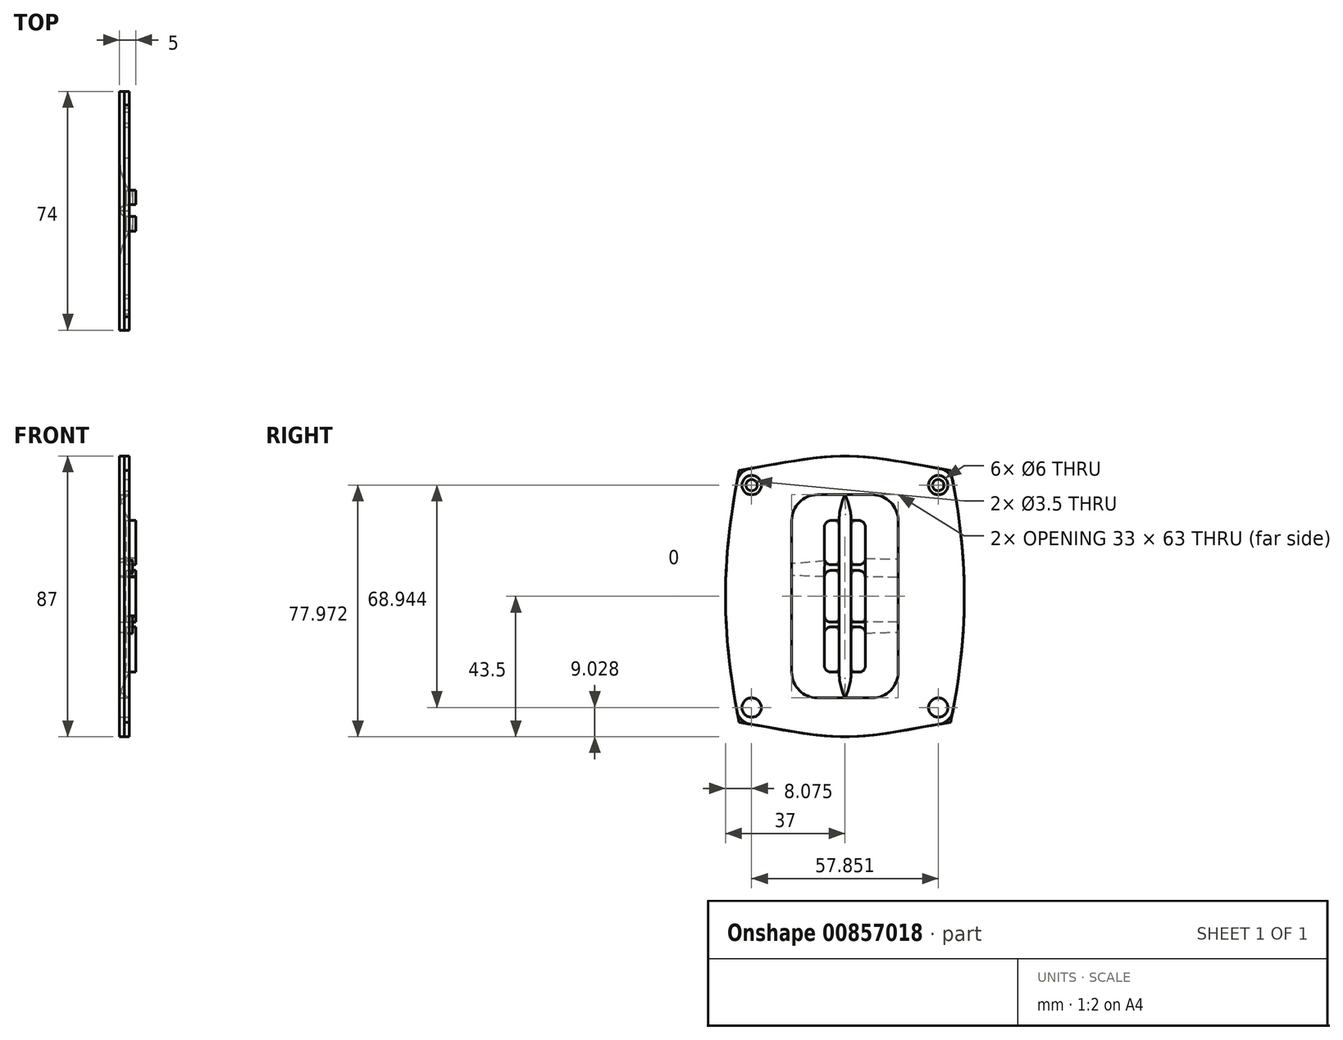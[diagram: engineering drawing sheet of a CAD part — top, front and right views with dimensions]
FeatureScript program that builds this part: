
annotation { "Feature Type Name" : "Feature", "Feature Type Description" : "" }
export const myFeature = defineFeature(function(context is Context, id is Id, definition is map)
    precondition{}
    {
        {
            var Q0;
            Q0=qCreatedBy(makeId("Right.planeOp"),FACE);
            var sketch = newSketch(context, id + "F0", { "sketchPlane" : qUnion([Q0])});
            skLineSegment(sketch, "E0", {"start": v(0, 0) * mm, "end": v(0, 31.5) * mm});
            skPoint(sketch, "E1.center", {"position": v(0, 0) * mm});
            skLineSegment(sketch, "E2", {"start": v(0, 0) * mm, "end": v(0, -31.5) * mm});
            skLineSegment(sketch, "E3.bottom", {"start": v(8.5, 31.5) * mm, "end": v(-8.5, 31.5) * mm});
            skLineSegment(sketch, "E3.top", {"start": v(8.5, -31.5) * mm, "end": v(-8.5, -31.5) * mm});
            skLineSegment(sketch, "E3.left", {"start": v(16.5, 23.5) * mm, "end": v(16.5, -23.5) * mm});
            skLineSegment(sketch, "E3.right", {"start": v(-16.5, 23.5) * mm, "end": v(-16.5, -23.5) * mm});
            skLineSegment(sketch, "E4.bottom", {"start": v(4.28, 8) * mm, "end": v(2.98, 8) * mm});
            skLineSegment(sketch, "E4.top", {"start": v(6.28, -8) * mm, "end": v(2.98, -8) * mm});
            skLineSegment(sketch, "E4.left", {"start": v(6.28, 6) * mm, "end": v(6.28, -8) * mm});
            skPoint(sketch, "E5.orphan", {"position": v(2.98, -17) * mm});
            skPoint(sketch, "E6.visualSharp", {"position": v(16.5, 31.5) * mm});
            skArc(sketch, "E6.filletArc", {"start": v(16.5, 23.5) * mm, "mid": v(14.16, 29.16) * mm, "end": v(8.5, 31.5) * mm});
            skPoint(sketch, "E7.visualSharp", {"position": v(-16.5, -31.5) * mm});
            skArc(sketch, "E7.filletArc", {"start": v(-16.5, -23.5) * mm, "mid": v(-14.16, -29.16) * mm, "end": v(-8.5, -31.5) * mm});
            skPoint(sketch, "E8.visualSharp", {"position": v(-16.5, 31.5) * mm});
            skArc(sketch, "E8.filletArc", {"start": v(-8.5, 31.5) * mm, "mid": v(-14.16, 29.16) * mm, "end": v(-16.5, 23.5) * mm});
            skPoint(sketch, "E9.visualSharp", {"position": v(16.5, -31.5) * mm});
            skArc(sketch, "E9.filletArc", {"start": v(8.5, -31.5) * mm, "mid": v(14.16, -29.16) * mm, "end": v(16.5, -23.5) * mm});
            skLineSegment(sketch, "E10.bottom", {"start": v(4.35, 23.5) * mm, "end": v(1.93, 23.5) * mm});
            skLineSegment(sketch, "E10.top", {"start": v(4.35, -23.5) * mm, "end": v(1.93, -23.5) * mm});
            skLineSegment(sketch, "E10.left", {"start": v(6.35, 21.5) * mm, "end": v(6.35, 11.8) * mm});
            skLineSegment(sketch, "E10.right", {"start": v(-6.35, 21.5) * mm, "end": v(-6.35, 11.8) * mm});
            skLineSegment(sketch, "E11", {"start": v(1.93, 23.5) * mm, "end": v(1.93, -23.5) * mm});
            skLineSegment(sketch, "E12", {"start": v(-1.78, -23.5) * mm, "end": v(-1.78, 23.5) * mm});
            skLineSegment(sketch, "E13", {"start": v(4.35, 9.8) * mm, "end": v(1.93, 9.8) * mm});
            skLineSegment(sketch, "E14", {"start": v(2.98, 8) * mm, "end": v(1.93, 8) * mm});
            skLineSegment(sketch, "E15", {"start": v(6.28, -8) * mm, "end": v(1.93, -8) * mm});
            skLineSegment(sketch, "E16", {"start": v(4.35, -9.47) * mm, "end": v(1.93, -9.47) * mm});
            skArc(sketch, "E17", {"start": v(1.93, 23.5) * mm, "mid": v(1.44, 27.61) * mm, "end": v(0, 31.5) * mm});
            skArc(sketch, "E18", {"start": v(0, 31.5) * mm, "mid": v(-1.33, 27.6) * mm, "end": v(-1.78, 23.5) * mm});
            skArc(sketch, "E19", {"start": v(-1.78, -23.5) * mm, "mid": v(-1.33, -27.6) * mm, "end": v(0, -31.5) * mm});
            skArc(sketch, "E20", {"start": v(0, -31.5) * mm, "mid": v(1.44, -27.61) * mm, "end": v(1.93, -23.5) * mm});
            skPoint(sketch, "E21.visualSharp", {"position": v(6.35, -23.5) * mm});
            skArc(sketch, "E21.filletArc", {"start": v(4.35, -23.5) * mm, "mid": v(5.76, -22.91) * mm, "end": v(6.35, -21.5) * mm});
            skPoint(sketch, "E22.visualSharp", {"position": v(-6.35, -23.5) * mm});
            skArc(sketch, "E22.filletArc", {"start": v(-6.35, -21.5) * mm, "mid": v(-5.76, -22.91) * mm, "end": v(-4.35, -23.5) * mm});
            skPoint(sketch, "E23.visualSharp", {"position": v(-6.35, 23.5) * mm});
            skArc(sketch, "E23.filletArc", {"start": v(-4.35, 23.5) * mm, "mid": v(-5.76, 22.91) * mm, "end": v(-6.35, 21.5) * mm});
            skPoint(sketch, "E24.visualSharp", {"position": v(6.35, 23.5) * mm});
            skArc(sketch, "E24.filletArc", {"start": v(6.35, 21.5) * mm, "mid": v(5.76, 22.91) * mm, "end": v(4.35, 23.5) * mm});
            skLineSegment(sketch, "E25.trimOffspring", {"start": v(-6.35, 6) * mm, "end": v(-6.35, -6) * mm});
            skLineSegment(sketch, "E26.trimOffspring", {"start": v(-1.78, 8) * mm, "end": v(-4.35, 8) * mm});
            skLineSegment(sketch, "E27.trimOffspring", {"start": v(-1.78, 9.8) * mm, "end": v(-4.35, 9.8) * mm});
            skLineSegment(sketch, "E28.trimOffspring", {"start": v(6.35, -11.47) * mm, "end": v(6.35, -21.5) * mm});
            skLineSegment(sketch, "E29.trimOffspring", {"start": v(-1.78, 23.5) * mm, "end": v(-4.35, 23.5) * mm});
            skLineSegment(sketch, "E30.trimOffspring", {"start": v(-6.35, -11.47) * mm, "end": v(-6.35, -21.5) * mm});
            skLineSegment(sketch, "E31.trimOffspring", {"start": v(-1.78, -8) * mm, "end": v(-4.35, -8) * mm});
            skLineSegment(sketch, "E32.trimOffspring", {"start": v(-1.78, -9.47) * mm, "end": v(-4.35, -9.47) * mm});
            skLineSegment(sketch, "E33.trimOffspring", {"start": v(-1.78, -23.5) * mm, "end": v(-4.35, -23.5) * mm});
            skPoint(sketch, "E34.visualSharp", {"position": v(6.35, -9.47) * mm});
            skArc(sketch, "E34.filletArc", {"start": v(6.35, -11.47) * mm, "mid": v(5.76, -10.05) * mm, "end": v(4.35, -9.47) * mm});
            skPoint(sketch, "E35.visualSharp", {"position": v(6.28, 8) * mm});
            skArc(sketch, "E35.filletArc", {"start": v(6.28, 6) * mm, "mid": v(5.7, 7.41) * mm, "end": v(4.28, 8) * mm});
            skPoint(sketch, "E36.visualSharp", {"position": v(-6.35, 8) * mm});
            skArc(sketch, "E36.filletArc", {"start": v(-4.35, 8) * mm, "mid": v(-5.76, 7.41) * mm, "end": v(-6.35, 6) * mm});
            skPoint(sketch, "E37.visualSharp", {"position": v(6.35, 9.8) * mm});
            skArc(sketch, "E37.filletArc", {"start": v(4.35, 9.8) * mm, "mid": v(5.76, 10.39) * mm, "end": v(6.35, 11.8) * mm});
            skPoint(sketch, "E38.visualSharp", {"position": v(-6.35, 9.8) * mm});
            skArc(sketch, "E38.filletArc", {"start": v(-6.35, 11.8) * mm, "mid": v(-5.76, 10.39) * mm, "end": v(-4.35, 9.8) * mm});
            skPoint(sketch, "E39.visualSharp", {"position": v(-6.35, -9.47) * mm});
            skArc(sketch, "E39.filletArc", {"start": v(-4.35, -9.47) * mm, "mid": v(-5.76, -10.05) * mm, "end": v(-6.35, -11.47) * mm});
            skPoint(sketch, "E40.visualSharp", {"position": v(-6.35, -8) * mm});
            skArc(sketch, "E40.filletArc", {"start": v(-6.35, -6) * mm, "mid": v(-5.76, -7.41) * mm, "end": v(-4.35, -8) * mm});
            skLineSegment(sketch, "E41", {"start": v(6.35, 11.8) * mm, "end": v(6.28, 6) * mm});
            skLineSegment(sketch, "E42", {"start": v(-6.22, 11.09) * mm, "end": v(-6.35, 6) * mm});
            skLineSegment(sketch, "E43", {"start": v(6.28, -8) * mm, "end": v(6.35, -11.47) * mm});
            skLineSegment(sketch, "E44", {"start": v(-6.35, -6) * mm, "end": v(-6.35, -6.14) * mm});
            skPoint(sketch, "E45", {"position": v(0, 43.5) * mm});
            skPoint(sketch, "E46", {"position": v(0, -43.5) * mm});
            skPoint(sketch, "E47", {"position": v(-37, 0) * mm});
            skPoint(sketch, "E48", {"position": v(37, 0) * mm});
            skLineSegment(sketch, "E49", {"start": v(6.3, 7.5) * mm, "end": v(5.95, 7.1) * mm});
            skPoint(sketch, "E50", {"position": v(28.93, 34.47) * mm});
            skCircle(sketch, "E51", {"center": v(28.93, 34.47) * mm, "radius": 3 * mm});
            skCircle(sketch, "E52", {"center": v(-28.93, 34.47) * mm, "radius": 3 * mm});
            skLineSegment(sketch, "E53", {"start": v(0, 0) * mm, "end": v(-1.78, 0) * mm});
            skLineSegment(sketch, "E54", {"start": v(-1, 0) * mm, "end": v(1.93, 0) * mm});
            skPoint(sketch, "E55.MirrorP", {"position": v(28.93, -34.47) * mm});
            skCircle(sketch, "E56.MirrorC", {"center": v(-28.93, -34.47) * mm, "radius": 3 * mm});
            skCircle(sketch, "E57.MirrorC", {"center": v(28.93, -34.47) * mm, "radius": 3 * mm});
            skPoint(sketch, "E58", {"position": v(32.78, 39.07) * mm});
            skPoint(sketch, "E59.MirrorP", {"position": v(-32.78, 39.07) * mm});
            skPoint(sketch, "E60.MirrorP", {"position": v(32.78, -39.07) * mm});
            skLineSegment(sketch, "E61", {"start": v(-6, 7.14) * mm, "end": v(-6.31, 7.52) * mm});
            skPoint(sketch, "E62.MirrorP", {"position": v(-32.78, -39.07) * mm});
            skFitSpline(sketch, "E63", {"points": [v(32.78, 39.07) * mm, v(0, 43.5) * mm, v(-32.78, 39.07) * mm], "startDerivative": vector(-65.56, 9.7) * mm, "endDerivative": vector(-65.56, -9.7) * mm});
            skFitSpline(sketch, "E64", {"points": [v(-32.78, 39.07) * mm, v(-37, 0) * mm, v(-32.78, -39.07) * mm], "startDerivative": vector(-15.65, -78.14) * mm, "endDerivative": vector(15.65, -78.14) * mm});
            skFitSpline(sketch, "E65", {"points": [v(-32.78, -39.07) * mm, v(0, -43.5) * mm, v(32.78, -39.07) * mm], "startDerivative": vector(65.56, -9.7) * mm, "endDerivative": vector(65.56, 9.7) * mm});
            skFitSpline(sketch, "E66", {"points": [v(32.78, -39.07) * mm, v(37, 0) * mm, v(32.78, 39.07) * mm], "startDerivative": vector(15.65, 78.14) * mm, "endDerivative": vector(-15.65, 78.14) * mm});
            skLineSegment(sketch, "E67", {"start": v(-6.35, -6) * mm, "end": v(-6.35, -12.75) * mm});
            skCircle(sketch, "E68", {"center": v(28.93, 34.47) * mm, "radius": 1.75 * mm});
            skCircle(sketch, "E69", {"center": v(-28.93, 34.47) * mm, "radius": 1.75 * mm});
            skCircle(sketch, "E70", {"center": v(28.93, -34.47) * mm, "radius": 1.75 * mm});
            skCircle(sketch, "E71", {"center": v(-28.93, -34.47) * mm, "radius": 1.75 * mm});
            skSolve(sketch);
        }
        {
            var Q0;
            {var subQ15=sQuery(id+"F0.wireOp",EDGE,"E6.filletArc");Q0=makeQuery(id+"F0.imprint","IMPRINT",FACE,{"disambiguationData":[TD([[makeQuery(id+"F0.imprint","IMPRINT",EDGE,{"derivedFrom":subQ15}),-1.0]])]});}
            var Q1;
            {var subQ0=sQuery(id+"F0.wireOp",EDGE,"E8.filletArc");Q1=makeQuery(id+"F0.imprint","IMPRINT",FACE,{"disambiguationData":[TD([[makeQuery(id+"F0.imprint","IMPRINT",EDGE,{"derivedFrom":subQ0}),-1.0]])]});}
            var Q2;
            {var subQ1=sQuery(id+"F0.wireOp",EDGE,"0K8LcDmi-TPdW-6mqs-PaqG-IcpSsZEtbQrD");var subQ9=sQuery(id+"F0.wireOp",EDGE,"E52");var subQ10=makeQuery(id+"F0.imprint","INTERSECT",VERTEX,{"disambiguationData":[OD(1.0)],"derivedFrom":[subQ1,subQ9]});Q2=makeQuery(id+"F0.imprint","IMPRINT",FACE,{"disambiguationData":[TD([[makeQuery(id+"F0.imprint","IMPRINT",EDGE,{"disambiguationData":[TD([[subQ10,-1.0]])],"derivedFrom":subQ1}),1.0]])]});}
            var Q3;
            {var subQ5=sQuery(id+"F0.wireOp",EDGE,"0K8LcDmi-TPdW-6mqs-PaqG-IcpSsZEtbQrD");var subQ10=sQuery(id+"F0.wireOp",EDGE,"E52");var subQ11=makeQuery(id+"F0.imprint","INTERSECT",VERTEX,{"disambiguationData":[OD(1.0)],"derivedFrom":[subQ5,subQ10]});Q3=makeQuery(id+"F0.imprint","IMPRINT",FACE,{"disambiguationData":[TD([[makeQuery(id+"F0.imprint","IMPRINT",EDGE,{"disambiguationData":[TD([[subQ11,-1.0]])],"derivedFrom":subQ5}),-1.0]])]});}
            var Q4;
            {var subQ0=sQuery(id+"F0.wireOp",EDGE,"E64");var subQ1=sQuery(id+"F0.wireOp",EDGE,"3NlvXYQv-4iI8-wcnj-cC3w-IblLpaBuwml8");var subQ2=makeQuery(id+"F0.imprint","INTERSECT",VERTEX,{"derivedFrom":[subQ1,subQ0]});Q4=makeQuery(id+"F0.imprint","IMPRINT",FACE,{"disambiguationData":[TD([[makeQuery(id+"F0.imprint","IMPRINT",EDGE,{"disambiguationData":[TD([[subQ2,1.0]])],"derivedFrom":subQ1}),-1.0]])]});}
            var Q5;
            {var subQ0=sQuery(id+"F0.wireOp",EDGE,"E63");var subQ1=sQuery(id+"F0.wireOp",EDGE,"3NlvXYQv-4iI8-wcnj-cC3w-IblLpaBuwml8");var subQ2=makeQuery(id+"F0.imprint","INTERSECT",VERTEX,{"derivedFrom":[subQ1,subQ0]});Q5=makeQuery(id+"F0.imprint","IMPRINT",FACE,{"disambiguationData":[TD([[makeQuery(id+"F0.imprint","IMPRINT",EDGE,{"disambiguationData":[TD([[subQ2,-1.0]])],"derivedFrom":subQ1}),-1.0]])]});}
            var Q6;
            {var subQ0=sQuery(id+"F0.wireOp",EDGE,"E66");var subQ3=sQuery(id+"F0.wireOp",EDGE,"267631c7-10f3-4b97-812b-e8a0e6330f70.trimOffspring");var subQ5=makeQuery(id+"F0.imprint","INTERSECT",VERTEX,{"derivedFrom":[subQ0,subQ3]});Q6=makeQuery(id+"F0.imprint","IMPRINT",FACE,{"disambiguationData":[TD([[makeQuery(id+"F0.imprint","IMPRINT",EDGE,{"disambiguationData":[TD([[subQ5,-1.0]])],"derivedFrom":subQ3}),-1.0]])]});}
            var Q7;
            {var subQ0=sQuery(id+"F0.wireOp",EDGE,"E63");var subQ3=sQuery(id+"F0.wireOp",EDGE,"267631c7-10f3-4b97-812b-e8a0e6330f70.trimOffspring");var subQ5=makeQuery(id+"F0.imprint","INTERSECT",VERTEX,{"derivedFrom":[subQ0,subQ3]});Q7=makeQuery(id+"F0.imprint","IMPRINT",FACE,{"disambiguationData":[TD([[makeQuery(id+"F0.imprint","IMPRINT",EDGE,{"disambiguationData":[TD([[subQ5,1.0]])],"derivedFrom":subQ3}),-1.0]])]});}
            var Q8;
            {var subQ5=sQuery(id+"F0.wireOp",EDGE,"E3.right");var subQ8=sQuery(id+"F0.wireOp",EDGE,"E53");var subQ10=makeQuery(id+"F0.imprint","INTERSECT",VERTEX,{"derivedFrom":[subQ5,subQ8]});Q8=makeQuery(id+"F0.imprint","IMPRINT",FACE,{"disambiguationData":[TD([[makeQuery(id+"F0.imprint","IMPRINT",EDGE,{"disambiguationData":[TD([[subQ10,-1.0]])],"derivedFrom":subQ5}),-1.0]])]});}
            var Q9;
            {var subQ5=sQuery(id+"F0.wireOp",EDGE,"E54");var subQ7=sQuery(id+"F0.wireOp",EDGE,"E3.left");var subQ8=makeQuery(id+"F0.imprint","INTERSECT",VERTEX,{"derivedFrom":[subQ7,subQ5]});Q9=makeQuery(id+"F0.imprint","IMPRINT",FACE,{"disambiguationData":[TD([[makeQuery(id+"F0.imprint","IMPRINT",EDGE,{"disambiguationData":[TD([[subQ8,-1.0]])],"derivedFrom":subQ7}),1.0]])]});}
            var Q10;
            {var subQ0=sQuery(id+"F0.wireOp",EDGE,"E9.filletArc");Q10=makeQuery(id+"F0.imprint","IMPRINT",FACE,{"disambiguationData":[TD([[makeQuery(id+"F0.imprint","IMPRINT",EDGE,{"derivedFrom":subQ0}),-1.0]])]});}
            var Q11;
            {var subQ0=sQuery(id+"F0.wireOp",EDGE,"E7.filletArc");Q11=makeQuery(id+"F0.imprint","IMPRINT",FACE,{"disambiguationData":[TD([[makeQuery(id+"F0.imprint","IMPRINT",EDGE,{"derivedFrom":subQ0}),-1.0]])]});}
            var Q12;
            {var subQ0=sQuery(id+"F0.wireOp",EDGE,"E64");var subQ1=sQuery(id+"F0.wireOp",EDGE,"K7zyOE5i-nbKv-ZZG0-sWNs-M6NRllElzCo4");var subQ2=makeQuery(id+"F0.imprint","INTERSECT",VERTEX,{"derivedFrom":[subQ1,subQ0]});Q12=makeQuery(id+"F0.imprint","IMPRINT",FACE,{"disambiguationData":[TD([[makeQuery(id+"F0.imprint","IMPRINT",EDGE,{"disambiguationData":[TD([[subQ2,1.0]])],"derivedFrom":subQ1}),1.0]])]});}
            var Q13;
            {var subQ0=sQuery(id+"F0.wireOp",EDGE,"E64");var subQ1=sQuery(id+"F0.wireOp",EDGE,"K7zyOE5i-nbKv-ZZG0-sWNs-M6NRllElzCo4");var subQ2=makeQuery(id+"F0.imprint","INTERSECT",VERTEX,{"derivedFrom":[subQ1,subQ0]});Q13=makeQuery(id+"F0.imprint","IMPRINT",FACE,{"disambiguationData":[TD([[makeQuery(id+"F0.imprint","IMPRINT",EDGE,{"disambiguationData":[TD([[subQ2,1.0]])],"derivedFrom":subQ1}),-1.0]])]});}
            var Q14;
            {var subQ0=sQuery(id+"F0.wireOp",EDGE,"E65");var subQ3=sQuery(id+"F0.wireOp",EDGE,"654dab88-8538-4310-9f04-b9e335b89f10.trimOffspring");var subQ5=makeQuery(id+"F0.imprint","INTERSECT",VERTEX,{"derivedFrom":[subQ0,subQ3]});Q14=makeQuery(id+"F0.imprint","IMPRINT",FACE,{"disambiguationData":[TD([[makeQuery(id+"F0.imprint","IMPRINT",EDGE,{"disambiguationData":[TD([[subQ5,-1.0]])],"derivedFrom":subQ3}),-1.0]])]});}
            var Q15;
            {var subQ0=sQuery(id+"F0.wireOp",EDGE,"E66");var subQ3=sQuery(id+"F0.wireOp",EDGE,"654dab88-8538-4310-9f04-b9e335b89f10.trimOffspring");var subQ5=makeQuery(id+"F0.imprint","INTERSECT",VERTEX,{"derivedFrom":[subQ0,subQ3]});Q15=makeQuery(id+"F0.imprint","IMPRINT",FACE,{"disambiguationData":[TD([[makeQuery(id+"F0.imprint","IMPRINT",EDGE,{"disambiguationData":[TD([[subQ5,1.0]])],"derivedFrom":subQ3}),-1.0]])]});}
            var Q16;
            {var subQ3=sQuery(id+"F0.wireOp",EDGE,"E51");var subQ9=sQuery(id+"F0.wireOp",EDGE,"llN5oSnz-mlLl-dkxG-KH2I-GPJlLPWOUWDz");var subQ10=makeQuery(id+"F0.imprint","INTERSECT",VERTEX,{"disambiguationData":[OD(1.0)],"derivedFrom":[subQ9,subQ3]});Q16=makeQuery(id+"F0.imprint","IMPRINT",FACE,{"disambiguationData":[TD([[makeQuery(id+"F0.imprint","IMPRINT",EDGE,{"disambiguationData":[TD([[subQ10,-1.0]])],"derivedFrom":subQ9}),-1.0]])]});}
            var Q17;
            {var subQ9=sQuery(id+"F0.wireOp",EDGE,"0K8LcDmi-TPdW-6mqs-PaqG-IcpSsZEtbQrD");var subQ11=sQuery(id+"F0.wireOp",EDGE,"E64");var subQ12=makeQuery(id+"F0.imprint","INTERSECT",VERTEX,{"derivedFrom":[subQ9,subQ11]});Q17=makeQuery(id+"F0.imprint","IMPRINT",FACE,{"disambiguationData":[TD([[makeQuery(id+"F0.imprint","IMPRINT",EDGE,{"disambiguationData":[TD([[subQ12,1.0]])],"derivedFrom":subQ9}),1.0]])]});}
            var Q18;
            {var subQ5=sQuery(id+"F0.wireOp",EDGE,"E51");var subQ6=sQuery(id+"F0.wireOp",EDGE,"llN5oSnz-mlLl-dkxG-KH2I-GPJlLPWOUWDz");var subQ7=makeQuery(id+"F0.imprint","INTERSECT",VERTEX,{"disambiguationData":[OD(0.0)],"derivedFrom":[subQ6,subQ5]});Q18=makeQuery(id+"F0.imprint","IMPRINT",FACE,{"disambiguationData":[TD([[makeQuery(id+"F0.imprint","IMPRINT",EDGE,{"disambiguationData":[TD([[subQ7,1.0]])],"derivedFrom":subQ6}),-1.0]])]});}
            var Q19;
            {var subQ0=sQuery(id+"F0.wireOp",EDGE,"E51");var subQ1=sQuery(id+"F0.wireOp",EDGE,"llN5oSnz-mlLl-dkxG-KH2I-GPJlLPWOUWDz");var subQ2=makeQuery(id+"F0.imprint","INTERSECT",VERTEX,{"disambiguationData":[OD(1.0)],"derivedFrom":[subQ1,subQ0]});Q19=makeQuery(id+"F0.imprint","IMPRINT",FACE,{"disambiguationData":[TD([[makeQuery(id+"F0.imprint","IMPRINT",EDGE,{"disambiguationData":[TD([[subQ2,-1.0]])],"derivedFrom":subQ1}),1.0]])]});}
            var Q20;
            {var subQ0=sQuery(id+"F0.wireOp",EDGE,"E51");var subQ1=sQuery(id+"F0.wireOp",EDGE,"llN5oSnz-mlLl-dkxG-KH2I-GPJlLPWOUWDz");var subQ2=makeQuery(id+"F0.imprint","INTERSECT",VERTEX,{"disambiguationData":[OD(0.0)],"derivedFrom":[subQ1,subQ0]});Q20=makeQuery(id+"F0.imprint","IMPRINT",FACE,{"disambiguationData":[TD([[makeQuery(id+"F0.imprint","IMPRINT",EDGE,{"disambiguationData":[TD([[subQ2,1.0]])],"derivedFrom":subQ1}),1.0]])]});}
            var Q21;
            {var subQ5=sQuery(id+"F0.wireOp",EDGE,"E64");var subQ6=sQuery(id+"F0.wireOp",EDGE,"0K8LcDmi-TPdW-6mqs-PaqG-IcpSsZEtbQrD");var subQ7=makeQuery(id+"F0.imprint","INTERSECT",VERTEX,{"derivedFrom":[subQ6,subQ5]});Q21=makeQuery(id+"F0.imprint","IMPRINT",FACE,{"disambiguationData":[TD([[makeQuery(id+"F0.imprint","IMPRINT",EDGE,{"disambiguationData":[TD([[subQ7,1.0]])],"derivedFrom":subQ6}),-1.0]])]});}
            extrude(context, id + "F1", {"entities" : qUnion([Q0, Q1, Q2, Q3, Q4, Q5, Q6, Q7, Q8, Q9, Q10, Q11, Q12, Q13, Q14, Q15, Q16, Q17, Q18, Q19, Q20, Q21]), "oppositeDirection" : true, "depth" : 3 * mm, "offsetDistance" : 25 * mm});
        }
        {
            var Q0;
            Q0=makeQuery(id+"F0.imprint","IMPRINT",FACE,{"disambiguationData":[TD([[makeQuery(id+"F0.imprint","IMPRINT",EDGE,{"derivedFrom":sQuery(id+"F0.wireOp",EDGE,"E4.bottom")}),-1.0]])]});
            var Q1;
            {var subQ1=sQuery(id+"F0.wireOp",EDGE,"E26.trimOffspring");Q1=makeQuery(id+"F0.imprint","IMPRINT",FACE,{"disambiguationData":[TD([[makeQuery(id+"F0.imprint","IMPRINT",EDGE,{"derivedFrom":subQ1}),-1.0]])]});}
            var Q2;
            {var subQ4=sQuery(id+"F0.wireOp",EDGE,"E31.trimOffspring");Q2=makeQuery(id+"F0.imprint","IMPRINT",FACE,{"disambiguationData":[TD([[makeQuery(id+"F0.imprint","IMPRINT",EDGE,{"derivedFrom":subQ4}),1.0]])]});}
            var Q3;
            {var subQ0=sQuery(id+"F0.wireOp",EDGE,"E16");Q3=makeQuery(id+"F0.imprint","IMPRINT",FACE,{"disambiguationData":[TD([[makeQuery(id+"F0.imprint","IMPRINT",EDGE,{"derivedFrom":subQ0}),-1.0]])]});}
            var Q4;
            {var subQ3=sQuery(id+"F0.wireOp",EDGE,"E49");Q4=makeQuery(id+"F0.imprint","IMPRINT",FACE,{"disambiguationData":[TD([[makeQuery(id+"F0.imprint","IMPRINT",EDGE,{"derivedFrom":subQ3}),1.0]])]});}
            var Q5;
            {var subQ0=sQuery(id+"F0.wireOp",EDGE,"E61");Q5=makeQuery(id+"F0.imprint","IMPRINT",FACE,{"disambiguationData":[TD([[makeQuery(id+"F0.imprint","IMPRINT",EDGE,{"derivedFrom":subQ0}),1.0]])]});}
            extrude(context, id + "F2", {"entities" : qUnion([Q0, Q1, Q2, Q3, Q4, Q5]), "depth" : 1 * mm, "offsetDistance" : 25 * mm});
        }
        {
            var Q0;
            {var subQ0=sQuery(id+"F0.wireOp",EDGE,"E17");Q0=makeQuery(id+"F0.imprint","IMPRINT",FACE,{"disambiguationData":[TD([[makeQuery(id+"F0.imprint","IMPRINT",EDGE,{"derivedFrom":subQ0}),1.0]])]});}
            var Q1;
            {var subQ3=sQuery(id+"F0.wireOp",EDGE,"E18");Q1=makeQuery(id+"F0.imprint","IMPRINT",FACE,{"disambiguationData":[TD([[makeQuery(id+"F0.imprint","IMPRINT",EDGE,{"derivedFrom":subQ3}),1.0]])]});}
            var Q2;
            {var subQ6=sQuery(id+"F0.wireOp",EDGE,"E2");Q2=makeQuery(id+"F0.imprint","IMPRINT",FACE,{"disambiguationData":[TD([[makeQuery(id+"F0.imprint","IMPRINT",EDGE,{"derivedFrom":subQ6}),-1.0]])]});}
            var Q3;
            {var subQ6=sQuery(id+"F0.wireOp",EDGE,"E2");Q3=makeQuery(id+"F0.imprint","IMPRINT",FACE,{"disambiguationData":[TD([[makeQuery(id+"F0.imprint","IMPRINT",EDGE,{"derivedFrom":subQ6}),1.0]])]});}
            extrude(context, id + "F3", {"entities" : qUnion([Q0, Q1, Q2, Q3]), "oppositeDirection" : true, "depth" : 3 * mm, "offsetDistance" : 25 * mm, "hasDraft" : true, "draftAngle" : 15 * degree, "draftPullDirection" : true});
        }
        {
            var Q0;
            Q0=makeQuery(id+"F3.opExtrude","CAP_EDGE",EDGE,{"disambiguationData":[OSD([sQuery(id+"F0.wireOp",EDGE,"E11")])],"isStart":false});
            var Q1;
            Q1=makeQuery(id+"F3.opExtrude","CAP_EDGE",EDGE,{"disambiguationData":[OSD([sQuery(id+"F0.wireOp",EDGE,"E12")])],"isStart":false});
            fillet(context, id + "F4", {"entities" : qUnion([Q0, Q1]), "radius" : 1.25 * mm, "tangentPropagation" : true, "allowEdgeOverflow" : false});
        }
        {
            var Q0;
            Q0=makeQuery(id+"F0.imprint","IMPRINT",FACE,{"disambiguationData":[TD([[makeQuery(id+"F0.imprint","IMPRINT",EDGE,{"derivedFrom":sQuery(id+"F0.wireOp",EDGE,"E3.left")}),-1.0]])]});
            var Q1;
            Q1=makeQuery(id+"F0.imprint","IMPRINT",FACE,{"disambiguationData":[TD([[makeQuery(id+"F0.imprint","IMPRINT",EDGE,{"derivedFrom":sQuery(id+"F0.wireOp",EDGE,"E3.right")}),1.0]])]});
            var Q2;
            {var subQ5=sQuery(id+"F0.wireOp",EDGE,"E6.filletArc");Q2=makeQuery(id+"F0.imprint","IMPRINT",FACE,{"disambiguationData":[TD([[makeQuery(id+"F0.imprint","IMPRINT",EDGE,{"derivedFrom":subQ5}),1.0]])]});}
            var Q3;
            {var subQ9=sQuery(id+"F0.wireOp",EDGE,"E8.filletArc");Q3=makeQuery(id+"F0.imprint","IMPRINT",FACE,{"disambiguationData":[TD([[makeQuery(id+"F0.imprint","IMPRINT",EDGE,{"derivedFrom":subQ9}),1.0]])]});}
            extrude(context, id + "F5", {"entities" : qUnion([Q0, Q1, Q2, Q3]), "oppositeDirection" : true, "depth" : 3 * mm, "offsetDistance" : 25 * mm});
        }
        {
            var Q0;
            Q0=makeQuery(id+"F5.opExtrude","CAP_EDGE",EDGE,{"disambiguationData":[OSD([sQuery(id+"F0.wireOp",EDGE,"E25.trimOffspring")])],"isStart":false});
            var Q1;
            Q1=makeQuery(id+"F5.opExtrude","CAP_EDGE",EDGE,{"disambiguationData":[OSD([sQuery(id+"F0.wireOp",EDGE,"E30.trimOffspring")])],"isStart":false});
            var Q2;
            Q2=makeQuery(id+"F5.opExtrude","CAP_EDGE",EDGE,{"disambiguationData":[OSD([sQuery(id+"F0.wireOp",EDGE,"E10.right")])],"isStart":false});
            var Q3;
            Q3=makeQuery(id+"F5.opExtrude","CAP_EDGE",EDGE,{"disambiguationData":[OSD([sQuery(id+"F0.wireOp",EDGE,"E4.left")])],"isStart":false});
            var Q4;
            Q4=makeQuery(id+"F5.opExtrude","CAP_EDGE",EDGE,{"disambiguationData":[OSD([sQuery(id+"F0.wireOp",EDGE,"E10.left")])],"isStart":false});
            var Q5;
            Q5=makeQuery(id+"F5.opExtrude","CAP_EDGE",EDGE,{"disambiguationData":[OSD([sQuery(id+"F0.wireOp",EDGE,"E28.trimOffspring")])],"isStart":false});
            fillet(context, id + "F6", {"entities" : qUnion([Q0, Q1, Q2, Q3, Q4, Q5]), "radius" : 18.5 * mm, "tangentPropagation" : true, "allowEdgeOverflow" : false});
        }
        {
            var Q0;
            {var subQ2=sQuery(id+"F0.wireOp",EDGE,"E10.bottom");Q0=makeQuery(id+"F0.imprint","IMPRINT",FACE,{"disambiguationData":[TD([[makeQuery(id+"F0.imprint","IMPRINT",EDGE,{"derivedFrom":subQ2}),1.0]])]});}
            var Q1;
            {var subQ1=sQuery(id+"F0.wireOp",EDGE,"E10.right");Q1=makeQuery(id+"F0.imprint","IMPRINT",FACE,{"disambiguationData":[TD([[makeQuery(id+"F0.imprint","IMPRINT",EDGE,{"derivedFrom":subQ1}),1.0]])]});}
            var Q2;
            {var subQ6=sQuery(id+"F0.wireOp",EDGE,"E25.trimOffspring");Q2=makeQuery(id+"F0.imprint","IMPRINT",FACE,{"disambiguationData":[TD([[makeQuery(id+"F0.imprint","IMPRINT",EDGE,{"derivedFrom":subQ6}),1.0]])]});}
            var Q3;
            Q3=makeQuery(id+"F0.imprint","IMPRINT",FACE,{"disambiguationData":[TD([[makeQuery(id+"F0.imprint","IMPRINT",EDGE,{"derivedFrom":sQuery(id+"F0.wireOp",EDGE,"E4.bottom")}),1.0]])]});
            var Q4;
            {var subQ0=sQuery(id+"F0.wireOp",EDGE,"E10.top");Q4=makeQuery(id+"F0.imprint","IMPRINT",FACE,{"disambiguationData":[TD([[makeQuery(id+"F0.imprint","IMPRINT",EDGE,{"derivedFrom":subQ0}),-1.0]])]});}
            var Q5;
            Q5=makeQuery(id+"F0.imprint","IMPRINT",FACE,{"disambiguationData":[TD([[makeQuery(id+"F0.imprint","IMPRINT",EDGE,{"derivedFrom":sQuery(id+"F0.wireOp",EDGE,"E22.filletArc")}),1.0]])]});
            extrude(context, id + "F7", {"entities" : qUnion([Q0, Q1, Q2, Q3, Q4, Q5]), "depth" : 2 * mm, "offsetDistance" : 25 * mm});
        }
        {
            var Q0;
            Q0=makeQuery(id+"F1.opExtrude","SWEPT_EDGE",EDGE,{"disambiguationData":[OSD([sQuery(id+"F0.wireOp",EDGE,"CrqveTTU-tZFd-cXGs-8LNY-Oqor6saillMY"),sQuery(id+"F0.wireOp",EDGE,"E63"),sQuery(id+"F0.wireOp",EDGE,"E66")])]});
            var Q1;
            Q1=makeQuery(id+"F1.opExtrude","SWEPT_EDGE",EDGE,{"disambiguationData":[OSD([sQuery(id+"F0.wireOp",EDGE,"E61"),sQuery(id+"F0.wireOp",EDGE,"E63"),sQuery(id+"F0.wireOp",EDGE,"E64")])]});
            var Q2;
            Q2=makeQuery(id+"F1.opExtrude","SWEPT_EDGE",EDGE,{"disambiguationData":[OSD([sQuery(id+"F0.wireOp",EDGE,"E64"),sQuery(id+"F0.wireOp",EDGE,"E65")])]});
            var Q3;
            Q3=makeQuery(id+"F1.opExtrude","SWEPT_EDGE",EDGE,{"disambiguationData":[OSD([sQuery(id+"F0.wireOp",EDGE,"f4dcv4kQ-fGtj-r0nX-oZ0C-H4q2S16pXg31"),sQuery(id+"F0.wireOp",EDGE,"E65"),sQuery(id+"F0.wireOp",EDGE,"E66")])]});
            fillet(context, id + "F8", {"entities" : qUnion([Q0, Q1, Q2, Q3]), "radius" : 5 * mm, "tangentPropagation" : true, "allowEdgeOverflow" : false});
        }
        {
            var Q0;
            Q0=makeQuery(id+"F0.imprint","IMPRINT",FACE,{"disambiguationData":[TD([[makeQuery(id+"F0.imprint","IMPRINT",EDGE,{"derivedFrom":sQuery(id+"F0.wireOp",EDGE,"E51")}),1.0]])]});
            var Q1;
            Q1=makeQuery(id+"F0.imprint","IMPRINT",FACE,{"disambiguationData":[TD([[makeQuery(id+"F0.imprint","IMPRINT",EDGE,{"derivedFrom":sQuery(id+"F0.wireOp",EDGE,"E52")}),1.0]])]});
            var Q2;
            Q2=makeQuery(id+"F0.imprint","IMPRINT",FACE,{"disambiguationData":[TD([[makeQuery(id+"F0.imprint","IMPRINT",EDGE,{"derivedFrom":sQuery(id+"F0.wireOp",EDGE,"E56.MirrorC")}),-1.0]])]});
            var Q3;
            Q3=makeQuery(id+"F0.imprint","IMPRINT",FACE,{"disambiguationData":[TD([[makeQuery(id+"F0.imprint","IMPRINT",EDGE,{"derivedFrom":sQuery(id+"F0.wireOp",EDGE,"E57.MirrorC")}),-1.0]])]});
            extrude(context, id + "F9", {"entities" : qUnion([Q0, Q1, Q2, Q3]), "oppositeDirection" : true, "depth" : 1.5 * mm, "offsetDistance" : 25 * mm});
        }
        {
            var Q0;
            Q0=makeQuery(id+"F7.opExtrude","CAP_FACE",FACE,{"disambiguationData":[OSD([sQuery(id+"F0.wireOp",EDGE,"E10.bottom"),sQuery(id+"F0.wireOp",EDGE,"E10.left"),sQuery(id+"F0.wireOp",EDGE,"E11"),sQuery(id+"F0.wireOp",EDGE,"E13"),sQuery(id+"F0.wireOp",EDGE,"E24.filletArc"),sQuery(id+"F0.wireOp",EDGE,"E37.filletArc"),sQuery(id+"F0.wireOp",EDGE,"E41")])],"isStart":true});
            var Q1;
            Q1=makeQuery(id+"F7.opExtrude","CAP_FACE",FACE,{"disambiguationData":[OSD([sQuery(id+"F0.wireOp",EDGE,"E10.right"),sQuery(id+"F0.wireOp",EDGE,"E12"),sQuery(id+"F0.wireOp",EDGE,"E23.filletArc"),sQuery(id+"F0.wireOp",EDGE,"E27.trimOffspring"),sQuery(id+"F0.wireOp",EDGE,"E29.trimOffspring"),sQuery(id+"F0.wireOp",EDGE,"E38.filletArc")])],"isStart":true});
            var Q2;
            Q2=makeQuery(id+"F7.opExtrude","CAP_FACE",FACE,{"disambiguationData":[OSD([sQuery(id+"F0.wireOp",EDGE,"E12"),sQuery(id+"F0.wireOp",EDGE,"E22.filletArc"),sQuery(id+"F0.wireOp",EDGE,"E30.trimOffspring"),sQuery(id+"F0.wireOp",EDGE,"E32.trimOffspring"),sQuery(id+"F0.wireOp",EDGE,"E33.trimOffspring"),sQuery(id+"F0.wireOp",EDGE,"E39.filletArc"),sQuery(id+"F0.wireOp",EDGE,"E67")])],"isStart":true});
            var Q3;
            Q3=makeQuery(id+"F7.opExtrude","CAP_FACE",FACE,{"disambiguationData":[OSD([sQuery(id+"F0.wireOp",EDGE,"E10.top"),sQuery(id+"F0.wireOp",EDGE,"E11"),sQuery(id+"F0.wireOp",EDGE,"E16"),sQuery(id+"F0.wireOp",EDGE,"E21.filletArc"),sQuery(id+"F0.wireOp",EDGE,"E28.trimOffspring"),sQuery(id+"F0.wireOp",EDGE,"E34.filletArc"),sQuery(id+"F0.wireOp",EDGE,"E43")])],"isStart":true});
            var Q4;
            Q4=makeQuery(id+"F7.opExtrude","CAP_FACE",FACE,{"disambiguationData":[OSD([sQuery(id+"F0.wireOp",EDGE,"E4.bottom"),sQuery(id+"F0.wireOp",EDGE,"E4.left"),sQuery(id+"F0.wireOp",EDGE,"E11"),sQuery(id+"F0.wireOp",EDGE,"E14"),sQuery(id+"F0.wireOp",EDGE,"E35.filletArc"),sQuery(id+"F0.wireOp",EDGE,"E54")])],"isStart":true});
            var Q5;
            {var subQ1=sQuery(id+"F0.wireOp",EDGE,"E25.trimOffspring");Q5=makeQuery(id+"F0.imprint","IMPRINT",FACE,{"disambiguationData":[TD([[makeQuery(id+"F0.imprint","IMPRINT",EDGE,{"derivedFrom":subQ1}),1.0]])]});}
            extrude(context, id + "F10", {"entities" : qUnion([Q0, Q1, Q2, Q3, Q4, Q5]), "depth" : 1 * mm, "offsetDistance" : 25 * mm});
        }
        {
            var Q0;
            Q0=makeQuery(id+"F10.opExtrude","SWEPT_EDGE",EDGE,{"disambiguationData":[OSD([sQuery(id+"F0.wireOp",EDGE,"E4.left"),sQuery(id+"F0.wireOp",EDGE,"E15"),sQuery(id+"F0.wireOp",EDGE,"E43")])]});
            var Q1;
            Q1=makeQuery(id+"F10.opExtrude","SWEPT_EDGE",EDGE,{"disambiguationData":[OSD([sQuery(id+"F0.wireOp",EDGE,"E12"),sQuery(id+"F0.wireOp",EDGE,"E31.trimOffspring")])]});
            var Q2;
            Q2=makeQuery(id+"F10.opExtrude","SWEPT_EDGE",EDGE,{"disambiguationData":[OSD([sQuery(id+"F0.wireOp",EDGE,"E12"),sQuery(id+"F0.wireOp",EDGE,"E27.trimOffspring")])]});
            var Q3;
            Q3=makeQuery(id+"F10.opExtrude","SWEPT_EDGE",EDGE,{"disambiguationData":[OSD([sQuery(id+"F0.wireOp",EDGE,"E11"),sQuery(id+"F0.wireOp",EDGE,"E13")])]});
            var Q4;
            Q4=makeQuery(id+"F10.opExtrude","SWEPT_EDGE",EDGE,{"disambiguationData":[OSD([sQuery(id+"F0.wireOp",EDGE,"E11"),sQuery(id+"F0.wireOp",EDGE,"E15")])]});
            var Q5;
            Q5=makeQuery(id+"F10.opExtrude","SWEPT_EDGE",EDGE,{"disambiguationData":[OSD([sQuery(id+"F0.wireOp",EDGE,"E10.top"),sQuery(id+"F0.wireOp",EDGE,"E11"),sQuery(id+"F0.wireOp",EDGE,"E20")])]});
            var Q6;
            Q6=makeQuery(id+"F10.opExtrude","SWEPT_EDGE",EDGE,{"disambiguationData":[OSD([sQuery(id+"F0.wireOp",EDGE,"E12"),sQuery(id+"F0.wireOp",EDGE,"E19"),sQuery(id+"F0.wireOp",EDGE,"E33.trimOffspring")])]});
            var Q7;
            Q7=makeQuery(id+"F10.opExtrude","SWEPT_EDGE",EDGE,{"disambiguationData":[OSD([sQuery(id+"F0.wireOp",EDGE,"E10.bottom"),sQuery(id+"F0.wireOp",EDGE,"E11"),sQuery(id+"F0.wireOp",EDGE,"E17")])]});
            var Q8;
            Q8=makeQuery(id+"F10.opExtrude","SWEPT_EDGE",EDGE,{"disambiguationData":[OSD([sQuery(id+"F0.wireOp",EDGE,"E12"),sQuery(id+"F0.wireOp",EDGE,"E18"),sQuery(id+"F0.wireOp",EDGE,"E29.trimOffspring")])]});
            var Q9;
            Q9=makeQuery(id+"F10.opExtrude","SWEPT_EDGE",EDGE,{"disambiguationData":[OSD([sQuery(id+"F0.wireOp",EDGE,"E12"),sQuery(id+"F0.wireOp",EDGE,"E26.trimOffspring")])]});
            var Q10;
            Q10=makeQuery(id+"F10.opExtrude","SWEPT_EDGE",EDGE,{"disambiguationData":[OSD([sQuery(id+"F0.wireOp",EDGE,"E12"),sQuery(id+"F0.wireOp",EDGE,"E32.trimOffspring")])]});
            var Q11;
            Q11=makeQuery(id+"F10.opExtrude","SWEPT_EDGE",EDGE,{"disambiguationData":[OSD([sQuery(id+"F0.wireOp",EDGE,"E11"),sQuery(id+"F0.wireOp",EDGE,"E16")])]});
            var Q12;
            Q12=makeQuery(id+"F10.opExtrude","SWEPT_EDGE",EDGE,{"disambiguationData":[OSD([sQuery(id+"F0.wireOp",EDGE,"E11"),sQuery(id+"F0.wireOp",EDGE,"E14")])]});
            fillet(context, id + "F11", {"entities" : qUnion([Q0, Q1, Q2, Q3, Q4, Q5, Q6, Q7, Q8, Q9, Q10, Q11, Q12]), "radius" : 2 * mm, "tangentPropagation" : true, "allowEdgeOverflow" : false});
        }
    });
